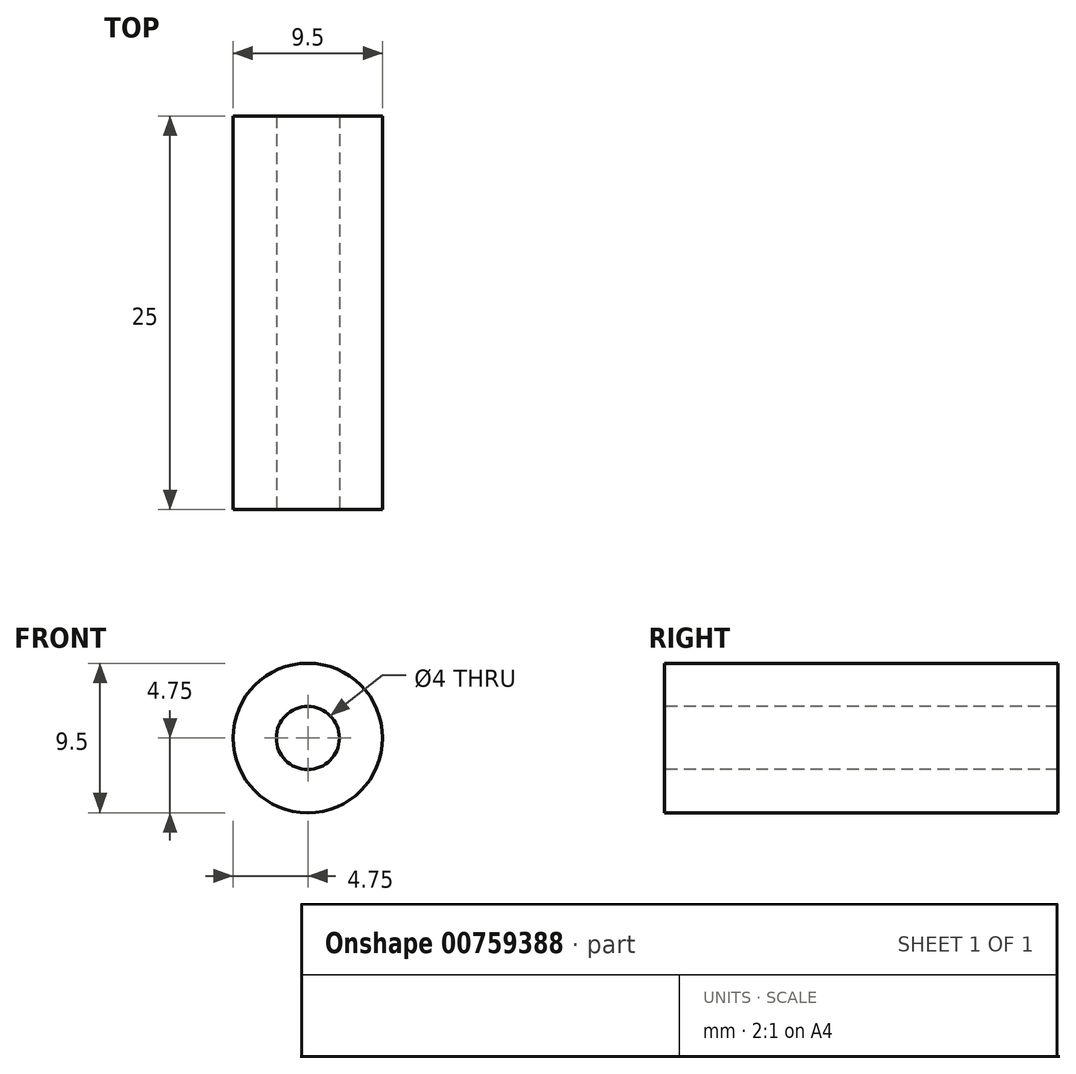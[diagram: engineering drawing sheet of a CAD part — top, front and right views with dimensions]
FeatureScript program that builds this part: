
annotation { "Feature Type Name" : "Feature", "Feature Type Description" : "" }
export const myFeature = defineFeature(function(context is Context, id is Id, definition is map)
    precondition{}
    {
        {
            var Q0;
            Q0=qCreatedBy(makeId("Front.planeOp"),FACE);
            var sketch = newSketch(context, id + "F0", { "sketchPlane" : qUnion([Q0])});
            skCircle(sketch, "E0", {"center": v(0, 0) * mm, "radius": 4.75 * mm});
            skCircle(sketch, "E1", {"center": v(0, 0) * mm, "radius": 2 * mm});
            skSolve(sketch);
        }
        {
            var Q0;
            Q0=makeQuery(id+"F0.imprint","IMPRINT",FACE,{"disambiguationData":[TD([[makeQuery(id+"F0.imprint","IMPRINT",EDGE,{"derivedFrom":sQuery(id+"F0.wireOp",EDGE,"E0")}),1.0]])]});
            extrude(context, id + "F1", {"entities" : qUnion([Q0]), "oppositeDirection" : true, "depth" : 25 * mm, "offsetDistance" : 25 * mm});
        }
    });
